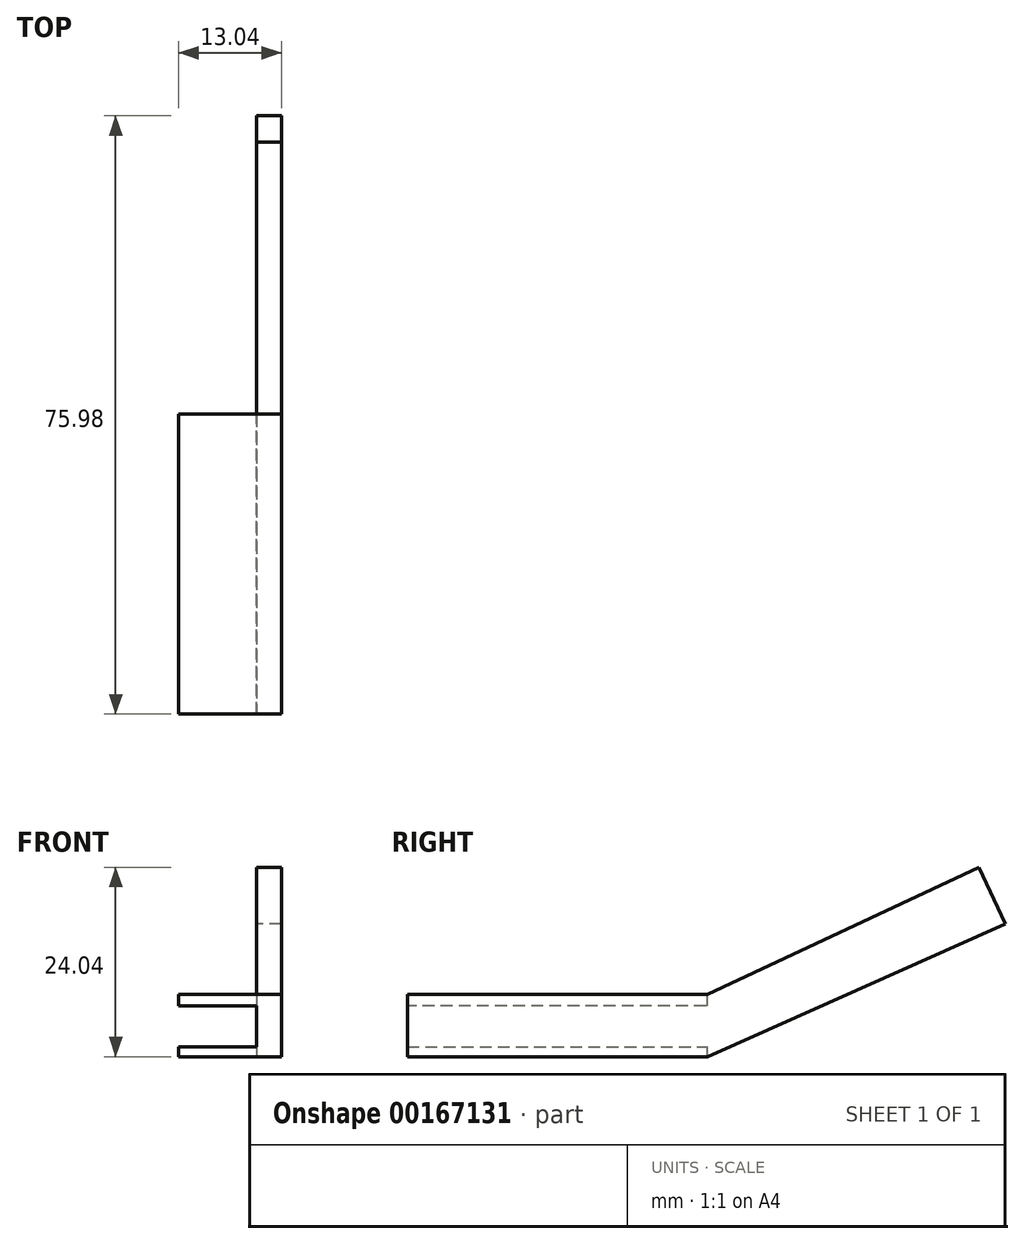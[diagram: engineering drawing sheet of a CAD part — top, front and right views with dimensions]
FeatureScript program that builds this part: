
annotation { "Feature Type Name" : "Feature", "Feature Type Description" : "" }
export const myFeature = defineFeature(function(context is Context, id is Id, definition is map)
    precondition{}
    {
        {
            var Q0;
            Q0=qCreatedBy(makeId("Right.planeOp"),FACE);
            var sketch = newSketch(context, id + "F0", { "sketchPlane" : qUnion([Q0])});
            skLineSegment(sketch, "E0.bottom", {"start": v(19.05, -3.97) * mm, "end": v(-19.05, -3.97) * mm});
            skLineSegment(sketch, "E0.top", {"start": v(19.05, 3.97) * mm, "end": v(-19.05, 3.97) * mm});
            skLineSegment(sketch, "E0.right", {"start": v(-19.05, -3.97) * mm, "end": v(-19.05, 3.97) * mm});
            skPoint(sketch, "E0.middle", {"position": v(0, 0) * mm});
            skLineSegment(sketch, "E1", {"start": v(19.05, 3.97) * mm, "end": v(53.58, 20.07) * mm});
            skLineSegment(sketch, "E2", {"start": v(53.58, 20.07) * mm, "end": v(56.93, 12.88) * mm});
            skLineSegment(sketch, "E3", {"start": v(56.93, 12.88) * mm, "end": v(19.05, -3.97) * mm});
            skSolve(sketch);
        }
        {
            var Q0;
            Q0=makeQuery(id+"F0.imprint","IMPRINT",FACE,{"disambiguationData":[TD([[makeQuery(id+"F0.imprint","IMPRINT",EDGE,{"derivedFrom":sQuery(id+"F0.wireOp",EDGE,"E0.bottom")}),-1.0]])]});
            extrude(context, id + "F1", {"entities" : qUnion([Q0]), "depth" : 31.75 * mm});
        }
        {
            var Q0;
            Q0=makeQuery(id+"F1.opExtrude","CAP_FACE",FACE,{"disambiguationData":[OSD([sQuery(id+"F0.wireOp",EDGE,"E0.bottom"),sQuery(id+"F0.wireOp",EDGE,"E0.top"),sQuery(id+"F0.wireOp",EDGE,"E0.right"),sQuery(id+"F0.wireOp",EDGE,"E1"),sQuery(id+"F0.wireOp",EDGE,"E2"),sQuery(id+"F0.wireOp",EDGE,"E3")])],"isStart":true});
            var sketch = newSketch(context, id + "F2", { "sketchPlane" : qUnion([Q0])});
            skLineSegment(sketch, "E4", {"start": v(-19.05, 3.97) * mm, "end": v(-19.05, -3.97) * mm});
            skLineSegment(sketch, "E5", {"start": v(-19.05, 3.97) * mm, "end": v(-19.05, 2.38) * mm});
            skLineSegment(sketch, "E6", {"start": v(-19.05, 2.38) * mm, "end": v(19.05, 2.38) * mm});
            skLineSegment(sketch, "E7", {"start": v(19.05, 2.38) * mm, "end": v(19.05, 3.97) * mm});
            skLineSegment(sketch, "E8", {"start": v(19.05, 3.97) * mm, "end": v(-19.05, 3.97) * mm});
            skLineSegment(sketch, "E9", {"start": v(-53.58, 20.07) * mm, "end": v(-19.05, 3.97) * mm});
            skLineSegment(sketch, "E10", {"start": v(-53.58, 20.07) * mm, "end": v(-54.25, 18.63) * mm});
            skLineSegment(sketch, "E11", {"start": v(-54.25, 18.63) * mm, "end": v(-19.05, 2.38) * mm});
            skLineSegment(sketch, "E12", {"start": v(-56.93, 12.88) * mm, "end": v(-56.26, 14.32) * mm});
            skLineSegment(sketch, "E13", {"start": v(-19.05, -3.97) * mm, "end": v(-19.05, -2.38) * mm});
            skLineSegment(sketch, "E14", {"start": v(-19.05, -2.38) * mm, "end": v(-56.26, 14.32) * mm});
            skLineSegment(sketch, "E15", {"start": v(-54.25, 18.63) * mm, "end": v(-56.26, 14.32) * mm});
            skLineSegment(sketch, "E16", {"start": v(19.05, -3.97) * mm, "end": v(19.05, -2.38) * mm});
            skLineSegment(sketch, "E17", {"start": v(19.05, -2.38) * mm, "end": v(-19.05, -2.38) * mm});
            skLineSegment(sketch, "E18", {"start": v(19.05, -2.38) * mm, "end": v(19.05, 2.38) * mm});
            skSolve(sketch);
        }
        {
            var Q0;
            Q0=makeQuery(id+"F1.opExtrude","CAP_FACE",FACE,{"disambiguationData":[OSD([sQuery(id+"F0.wireOp",EDGE,"E0.bottom"),sQuery(id+"F0.wireOp",EDGE,"E0.top"),sQuery(id+"F0.wireOp",EDGE,"E0.right"),sQuery(id+"F0.wireOp",EDGE,"E1"),sQuery(id+"F0.wireOp",EDGE,"E2"),sQuery(id+"F0.wireOp",EDGE,"E3")])],"isStart":true});
            var sketch = newSketch(context, id + "F3", { "sketchPlane" : qUnion([Q0])});
            skLineSegment(sketch, "E19", {"start": v(19.05, 3.97) * mm, "end": v(19.05, 2.38) * mm});
            skLineSegment(sketch, "E20", {"start": v(19.05, 2.38) * mm, "end": v(-19.05, 2.38) * mm});
            skLineSegment(sketch, "E21", {"start": v(-19.05, 2.38) * mm, "end": v(-19.05, -2.38) * mm});
            skLineSegment(sketch, "E22", {"start": v(-19.05, -2.38) * mm, "end": v(19.05, -2.38) * mm});
            skLineSegment(sketch, "E23", {"start": v(19.05, -2.38) * mm, "end": v(19.05, 2.38) * mm});
            skSolve(sketch);
        }
        {
            var Q0;
            Q0=makeQuery(id+"F3.imprint","IMPRINT",FACE,{"disambiguationData":[TD([[makeQuery(id+"F3.imprint","IMPRINT",EDGE,{"derivedFrom":sQuery(id+"F3.wireOp",EDGE,"E20")}),1.0]])]});
            extrude(context, id + "F4", {"entities" : qUnion([Q0]), "operationType" : NewBodyOperationType.REMOVE, "oppositeDirection" : true, "depth" : 28.57 * mm});
        }
        {
            var Q0;
            Q0=makeQuery(id+"F2.imprint","IMPRINT",FACE,{"disambiguationData":[TD([[makeQuery(id+"F2.imprint","IMPRINT",EDGE,{"derivedFrom":sQuery(id+"F2.wireOp",EDGE,"E4")}),-1.0]])]});
            extrude(context, id + "F5", {"entities" : qUnion([Q0]), "operationType" : NewBodyOperationType.REMOVE, "oppositeDirection" : true, "depth" : 28.57 * mm});
        }
        {
            var Q0;
            {var subQ0=sQuery(id+"F0.wireOp",EDGE,"E2");var subQ1=sQuery(id+"F0.wireOp",EDGE,"E1");var subQ2=sQuery(id+"F0.wireOp",EDGE,"E0.right");var subQ3=sQuery(id+"F0.wireOp",EDGE,"E0.top");Q0=makeQuery(id+"F5.boolean.opBoolean","SPLIT",FACE,{"disambiguationData":[TD([makeQuery(id+"F1.opExtrude","SWEPT_FACE",FACE,{"disambiguationData":[OSD([subQ3])]})])],"derivedFrom":makeQuery(id+"F1.opExtrude","CAP_FACE",FACE,{"disambiguationData":[OSD([sQuery(id+"F0.wireOp",EDGE,"E0.bottom"),subQ3,subQ2,subQ1,subQ0,sQuery(id+"F0.wireOp",EDGE,"E3")])],"isStart":true})});}
            var sketch = newSketch(context, id + "F6", { "sketchPlane" : qUnion([Q0])});
            skLineSegment(sketch, "E24", {"start": v(-54.19, 18.77) * mm, "end": v(-18.69, 2.38) * mm});
            skLineSegment(sketch, "E25", {"start": v(-18.69, 2.38) * mm, "end": v(-19.05, 2.38) * mm});
            skLineSegment(sketch, "E26", {"start": v(-19.05, 2.38) * mm, "end": v(-54.25, 18.63) * mm});
            skLineSegment(sketch, "E27", {"start": v(-54.25, 18.63) * mm, "end": v(-54.19, 18.77) * mm});
            skSolve(sketch);
        }
        {
            var Q0;
            Q0 = qSketchRegion(id + "F6", true);
            extrude(context, id + "F7", {"entities" : qUnion([Q0]), "operationType" : NewBodyOperationType.REMOVE, "oppositeDirection" : true, "depth" : 28.57 * mm});
        }
        {
            var Q0;
            {var subQ0=sQuery(id+"F0.wireOp",EDGE,"E2");var subQ1=sQuery(id+"F0.wireOp",EDGE,"E1");var subQ2=sQuery(id+"F0.wireOp",EDGE,"E0.right");var subQ3=sQuery(id+"F0.wireOp",EDGE,"E0.top");Q0=makeQuery(id+"F5.boolean.opBoolean","SPLIT",FACE,{"disambiguationData":[TD([makeQuery(id+"F1.opExtrude","SWEPT_FACE",FACE,{"disambiguationData":[OSD([subQ3])]})])],"derivedFrom":makeQuery(id+"F1.opExtrude","CAP_FACE",FACE,{"disambiguationData":[OSD([sQuery(id+"F0.wireOp",EDGE,"E0.bottom"),subQ3,subQ2,subQ1,subQ0,sQuery(id+"F0.wireOp",EDGE,"E3")])],"isStart":true})});}
            var sketch = newSketch(context, id + "F8", { "sketchPlane" : qUnion([Q0])});
            skLineSegment(sketch, "E28", {"start": v(-18.9, 2.47) * mm, "end": v(19.05, 2.47) * mm});
            skLineSegment(sketch, "E29", {"start": v(19.05, 2.47) * mm, "end": v(19.05, 2.38) * mm});
            skLineSegment(sketch, "E30", {"start": v(19.05, 2.38) * mm, "end": v(-18.69, 2.38) * mm});
            skLineSegment(sketch, "E31", {"start": v(-18.69, 2.38) * mm, "end": v(-18.9, 2.47) * mm});
            skSolve(sketch);
        }
        {
            var Q0;
            Q0 = qSketchRegion(id + "F8", true);
            extrude(context, id + "F9", {"entities" : qUnion([Q0]), "operationType" : NewBodyOperationType.REMOVE, "oppositeDirection" : true, "depth" : 28.57 * mm});
        }
        {
            var Q0;
            Q0=makeQuery(id+"F1.opExtrude","SWEPT_FACE",FACE,{"disambiguationData":[OSD([sQuery(id+"F0.wireOp",EDGE,"E0.top")])]});
            var sketch = newSketch(context, id + "F10", { "sketchPlane" : qUnion([Q0])});
            skLineSegment(sketch, "E32", {"start": v(18.71, -19.05) * mm, "end": v(18.71, 19.05) * mm});
            skLineSegment(sketch, "E33", {"start": v(18.71, 19.05) * mm, "end": v(0, 19.05) * mm});
            skLineSegment(sketch, "E34", {"start": v(0, 19.05) * mm, "end": v(0, -19.05) * mm});
            skLineSegment(sketch, "E35", {"start": v(0, -19.05) * mm, "end": v(18.71, -19.05) * mm});
            skSolve(sketch);
        }
        {
            var Q0;
            Q0 = qSketchRegion(id + "F10", true);
            extrude(context, id + "F11", {"entities" : qUnion([Q0]), "operationType" : NewBodyOperationType.REMOVE, "endBound" : BoundingType.THROUGH_ALL, "oppositeDirection" : true, "depth" : 25.4 * mm});
        }
        {
            var Q0;
            Q0=makeQuery(id+"F1.opExtrude","SWEPT_FACE",FACE,{"disambiguationData":[OSD([sQuery(id+"F0.wireOp",EDGE,"E1")])]});
            var sketch = newSketch(context, id + "F12", { "sketchPlane" : qUnion([Q0])});
            skLineSegment(sketch, "E36", {"start": v(18.71, 18.94) * mm, "end": v(18.71, 57.04) * mm});
            skLineSegment(sketch, "E37", {"start": v(18.71, 57.04) * mm, "end": v(0, 57.04) * mm});
            skLineSegment(sketch, "E38", {"start": v(0, 57.04) * mm, "end": v(0, 18.94) * mm});
            skLineSegment(sketch, "E39", {"start": v(0, 18.94) * mm, "end": v(18.71, 18.94) * mm});
            skSolve(sketch);
        }
        {
            var Q0;
            Q0 = qSketchRegion(id + "F12", true);
            extrude(context, id + "F13", {"entities" : qUnion([Q0]), "operationType" : NewBodyOperationType.REMOVE, "endBound" : BoundingType.THROUGH_ALL, "oppositeDirection" : true, "depth" : 25.4 * mm});
        }
        {
            var Q0;
            Q0=makeQuery(id+"F1.opExtrude","SWEPT_FACE",FACE,{"disambiguationData":[OSD([sQuery(id+"F0.wireOp",EDGE,"E3")])]});
            var sketch = newSketch(context, id + "F14", { "sketchPlane" : qUnion([Q0])});
            skLineSegment(sketch, "E40", {"start": v(18.71, -19.15) * mm, "end": v(18.71, -15.8) * mm});
            skLineSegment(sketch, "E41", {"start": v(18.71, -15.8) * mm, "end": v(0, -15.8) * mm});
            skLineSegment(sketch, "E42", {"start": v(0, -15.8) * mm, "end": v(0, -19.15) * mm});
            skLineSegment(sketch, "E43", {"start": v(0, -19.15) * mm, "end": v(18.71, -19.15) * mm});
            skSolve(sketch);
        }
        {
            var Q0;
            Q0 = qSketchRegion(id + "F14", true);
            extrude(context, id + "F15", {"entities" : qUnion([Q0]), "operationType" : NewBodyOperationType.REMOVE, "endBound" : BoundingType.THROUGH_ALL, "oppositeDirection" : true, "depth" : 25.4 * mm});
        }
        {
            var Q0;
            {var subQ0=makeQuery(id+"F1.opExtrude","SWEPT_FACE",FACE,{"disambiguationData":[OSD([sQuery(id+"F0.wireOp",EDGE,"E3")])]});Q0=makeQuery(id+"F15.boolean.opBoolean","MERGE",FACE,{"derivedFrom":[makeQuery(id+"F11.boolean.opBoolean","COPY",FACE,{"disambiguationData":[TD([makeQuery(id+"F1.opExtrude","SWEPT_FACE",FACE,{"disambiguationData":[OSD([sQuery(id+"F0.wireOp",EDGE,"E0.bottom")])]})])],"derivedFrom":makeQuery(id+"F11.opExtrude","SWEPT_FACE",FACE,{"disambiguationData":[OSD([sQuery(id+"F10.wireOp",EDGE,"E32")])]})}),makeQuery(id+"F13.boolean.opBoolean","COPY",FACE,{"disambiguationData":[TD([subQ0])],"derivedFrom":makeQuery(id+"F13.opExtrude","SWEPT_FACE",FACE,{"disambiguationData":[OSD([sQuery(id+"F12.wireOp",EDGE,"E36")])]})}),makeQuery(id+"F15.opExtrude","SWEPT_FACE",FACE,{"disambiguationData":[OSD([sQuery(id+"F14.wireOp",EDGE,"E40")])]})]});}
            var sketch = newSketch(context, id + "F16", { "sketchPlane" : qUnion([Q0])});
            skLineSegment(sketch, "E44", {"start": v(19.05, -2.71) * mm, "end": v(-19.05, -2.71) * mm});
            skLineSegment(sketch, "E45", {"start": v(-19.05, -2.71) * mm, "end": v(-56.45, 13.92) * mm});
            skLineSegment(sketch, "E46", {"start": v(-56.45, 13.92) * mm, "end": v(-56.26, 14.32) * mm});
            skLineSegment(sketch, "E47", {"start": v(-56.26, 14.32) * mm, "end": v(-19.05, -2.38) * mm});
            skLineSegment(sketch, "E48", {"start": v(-19.05, -2.38) * mm, "end": v(19.05, -2.38) * mm});
            skLineSegment(sketch, "E49", {"start": v(19.05, -2.38) * mm, "end": v(19.05, -2.71) * mm});
            skSolve(sketch);
        }
        {
            var Q0;
            Q0 = qSketchRegion(id + "F16", true);
            extrude(context, id + "F17", {"entities" : qUnion([Q0]), "operationType" : NewBodyOperationType.REMOVE, "oppositeDirection" : true, "depth" : 9.86 * mm});
        }
    });
